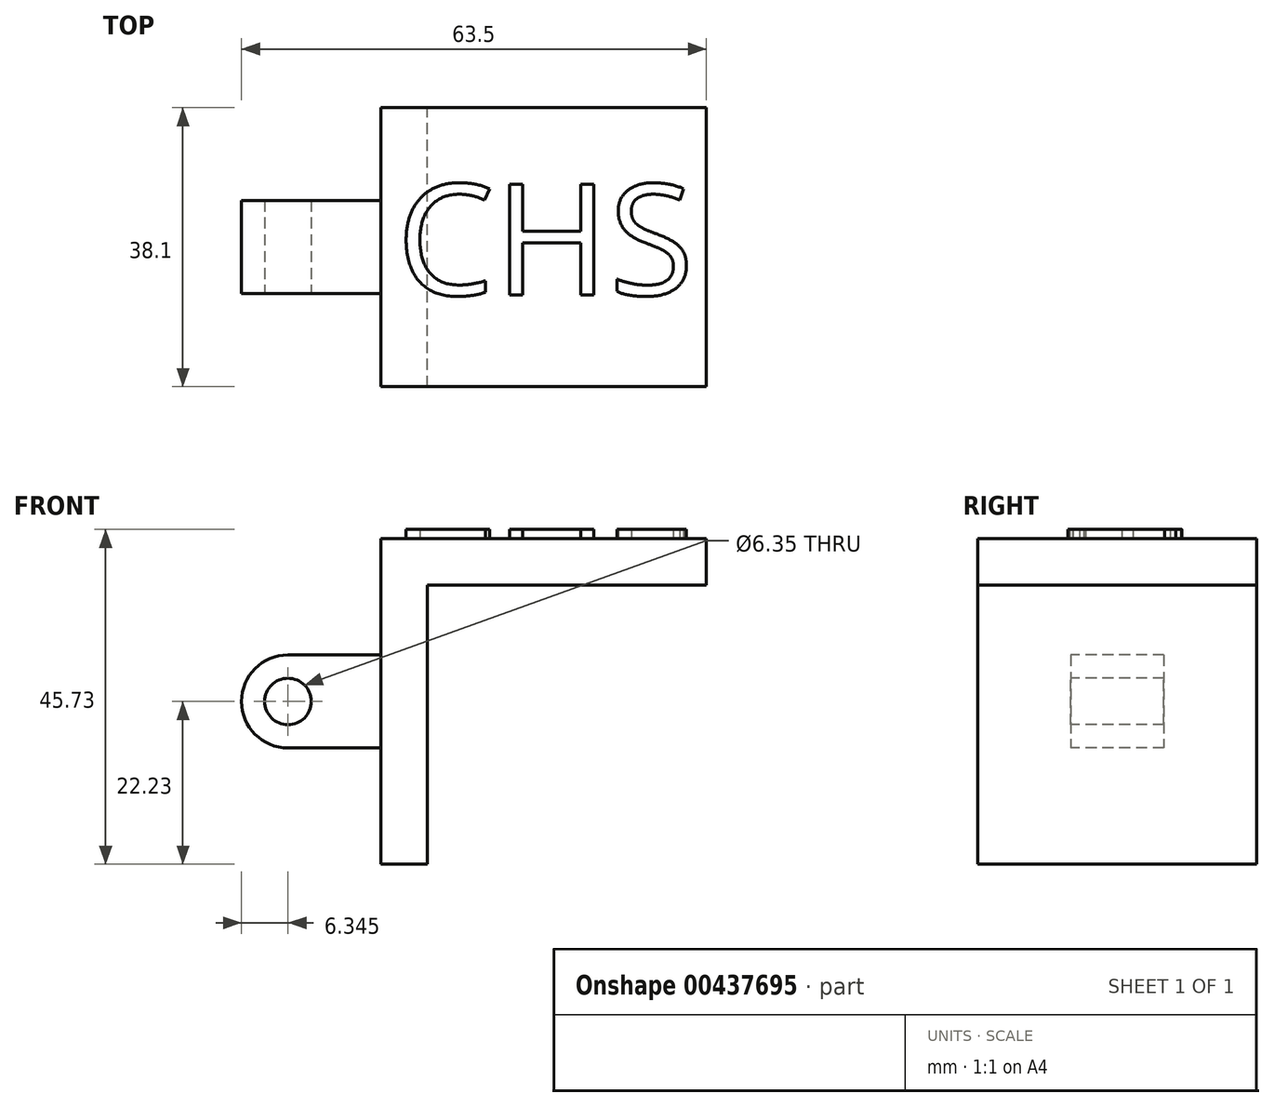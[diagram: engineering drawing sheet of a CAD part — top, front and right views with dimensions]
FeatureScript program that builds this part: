
annotation { "Feature Type Name" : "Feature", "Feature Type Description" : "" }
export const myFeature = defineFeature(function(context is Context, id is Id, definition is map)
    precondition{}
    {
        {
            var Q0;
            Q0=qCreatedBy(makeId("Front.planeOp"),FACE);
            var sketch = newSketch(context, id + "F0", { "sketchPlane" : qUnion([Q0])});
            skLineSegment(sketch, "E0.bottom", {"start": v(-22.22, 22.23) * mm, "end": v(22.23, 22.23) * mm});
            skLineSegment(sketch, "E0.top", {"start": v(-22.23, -22.22) * mm, "end": v(22.22, -22.22) * mm});
            skLineSegment(sketch, "E0.left", {"start": v(-22.22, 22.23) * mm, "end": v(-22.23, -22.22) * mm});
            skLineSegment(sketch, "E0.right", {"start": v(22.23, 22.23) * mm, "end": v(22.22, -22.22) * mm});
            skPoint(sketch, "E0.middle", {"position": v(0, 0) * mm});
            skLineSegment(sketch, "E1.bottom", {"start": v(22.22, -22.22) * mm, "end": v(-15.87, -22.22) * mm});
            skLineSegment(sketch, "E1.top", {"start": v(22.22, 15.88) * mm, "end": v(-15.88, 15.88) * mm});
            skLineSegment(sketch, "E1.left", {"start": v(22.22, -22.22) * mm, "end": v(22.22, 15.88) * mm});
            skLineSegment(sketch, "E1.right", {"start": v(-15.87, -22.23) * mm, "end": v(-15.88, 15.88) * mm});
            skSolve(sketch);
        }
        {
            var Q0;
            Q0=makeQuery(id+"F0.imprint","IMPRINT",FACE,{"disambiguationData":[TD([[makeQuery(id+"F0.imprint","IMPRINT",EDGE,{"derivedFrom":sQuery(id+"F0.wireOp",EDGE,"E0.bottom")}),-1.0]])]});
            extrude(context, id + "F1", {"entities" : qUnion([Q0]), "depth" : 38.1 * mm, "symmetric" : true});
        }
        {
            var Q0;
            Q0=makeQuery(id+"F1.opExtrude","SWEPT_FACE",FACE,{"disambiguationData":[OSD([sQuery(id+"F0.wireOp",EDGE,"E0.left")])]});
            var sketch = newSketch(context, id + "F2", { "sketchPlane" : qUnion([Q0])});
            skLineSegment(sketch, "E2.bottom", {"start": v(-6.35, 6.35) * mm, "end": v(6.35, 6.35) * mm});
            skLineSegment(sketch, "E2.top", {"start": v(-6.35, -6.35) * mm, "end": v(6.35, -6.35) * mm});
            skLineSegment(sketch, "E2.left", {"start": v(-6.35, 6.35) * mm, "end": v(-6.35, -6.35) * mm});
            skLineSegment(sketch, "E2.right", {"start": v(6.35, 6.35) * mm, "end": v(6.35, -6.35) * mm});
            skPoint(sketch, "E2.middle", {"position": v(0, 0) * mm});
            skSolve(sketch);
        }
        {
            var Q0;
            Q0=makeQuery(id+"F2.imprint","IMPRINT",FACE,{"disambiguationData":[TD([[makeQuery(id+"F2.imprint","IMPRINT",EDGE,{"derivedFrom":sQuery(id+"F2.wireOp",EDGE,"e7AB2JLP-uz8C-emsv-wjMX-BDqN4jFqbq5F")}),1.0]])]});
            var Q1;
            Q1=makeQuery(id+"F2.imprint","IMPRINT",FACE,{"disambiguationData":[TD([[makeQuery(id+"F2.imprint","IMPRINT",EDGE,{"derivedFrom":sQuery(id+"F2.wireOp",EDGE,"E2.bottom")}),-1.0]])]});
            extrude(context, id + "F3", {"entities" : qUnion([Q0, Q1]), "operationType" : NewBodyOperationType.ADD, "depth" : 19.05 * mm});
        }
        {
            var Q0;
            Q0=makeQuery(id+"F3.opExtrude","SWEPT_FACE",FACE,{"disambiguationData":[OSD([sQuery(id+"F2.wireOp",EDGE,"E2.right")])]});
            var sketch = newSketch(context, id + "F4", { "sketchPlane" : qUnion([Q0])});
            skCircle(sketch, "E3", {"center": v(-34.93, 0) * mm, "radius": 3.18 * mm});
            skPoint(sketch, "E3.centerSnap0", {"position": v(-41.28, 0) * mm});
            skSolve(sketch);
        }
        {
            var Q0;
            Q0=makeQuery(id+"F3.opExtrude","CAP_EDGE",EDGE,{"disambiguationData":[OSD([sQuery(id+"F2.wireOp",EDGE,"E2.bottom")])],"isStart":false});
            var Q1;
            Q1=makeQuery(id+"F3.opExtrude","CAP_EDGE",EDGE,{"disambiguationData":[OSD([sQuery(id+"F2.wireOp",EDGE,"E2.top")])],"isStart":false});
            fillet(context, id + "F5", {"entities" : qUnion([Q0, Q1]), "radius" : 6.35 * mm, "tangentPropagation" : true, "allowEdgeOverflow" : false});
        }
        {
            var Q0;
            Q0=makeQuery(id+"F4.imprint","IMPRINT",FACE,{"disambiguationData":[TD([[makeQuery(id+"F4.imprint","IMPRINT",EDGE,{"derivedFrom":sQuery(id+"F4.wireOp",EDGE,"E3")}),1.0]])]});
            extrude(context, id + "F6", {"entities" : qUnion([Q0]), "operationType" : NewBodyOperationType.REMOVE, "oppositeDirection" : true, "depth" : 25.4 * mm});
        }
        {
            var Q0;
            Q0=makeQuery(id+"F1.opExtrude","SWEPT_FACE",FACE,{"disambiguationData":[OSD([sQuery(id+"F0.wireOp",EDGE,"E0.bottom")])]});
            var sketch = newSketch(context, id + "F7", { "sketchPlane" : qUnion([Q0])});
            skText(sketch, "E4", { "text": "CHS", "fontName": "OpenSans-Regular.ttf"});
            const initialGuessF7  = {"E4": [-0.02007, -0.00653, 1, 0, 0.01524]};
            skSetInitialGuess(sketch, initialGuessF7);
            skSolve(sketch);
        }
        {
            var Q0;
            Q0 = qSketchRegion(id + "F7", true);
            var Q1;
            Q1 = qConstructionFilter(qBodyType(qCreatedBy(id + "F7" ,EDGE), BodyType.WIRE), ConstructionObject.NO);
            extrude(context, id + "F8", {"entities" : qUnion([Q0]), "surfaceEntities" : qUnion([Q1]), "depth" : 1.27 * mm});
        }
    });
